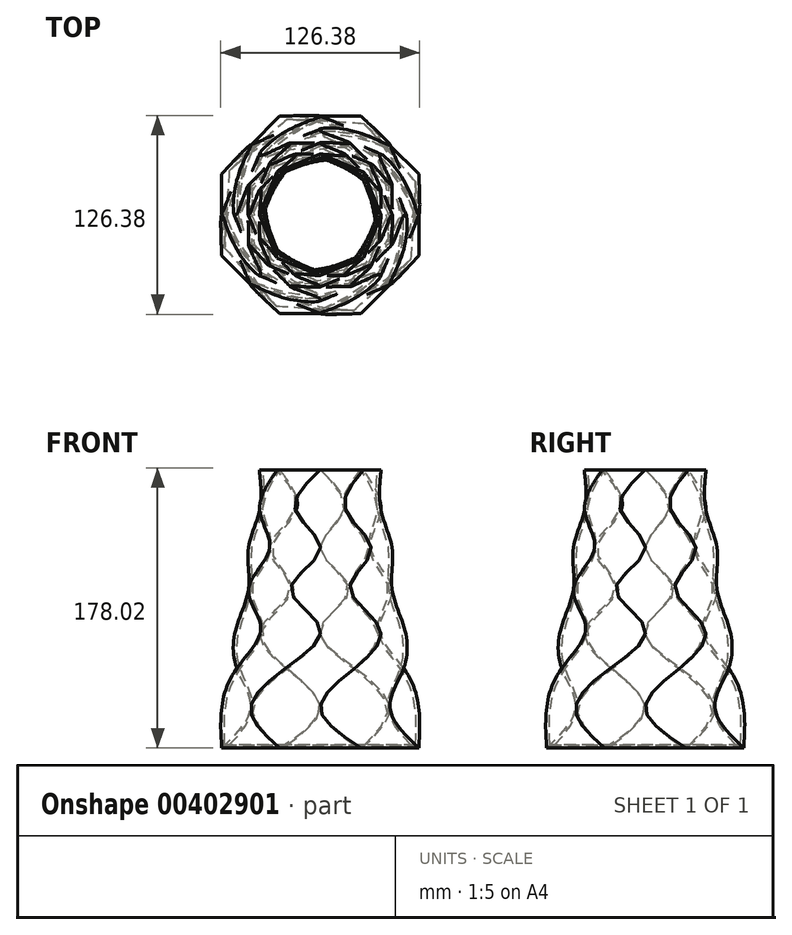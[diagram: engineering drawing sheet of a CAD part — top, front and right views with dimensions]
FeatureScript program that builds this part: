
annotation { "Feature Type Name" : "Feature", "Feature Type Description" : "" }
export const myFeature = defineFeature(function(context is Context, id is Id, definition is map)
    precondition{}
    {
        {
            var Q0;
            Q0=qCreatedBy(makeId("Top.planeOp"),FACE);
            var sketch = newSketch(context, id + "F0", { "sketchPlane" : qUnion([Q0])});
            skCircle(sketch, "E0.cCircle", {"center": v(0, 0) * mm, "radius": 62.6 * mm, "construction": true});
            skLineSegment(sketch, "E0.0", {"start": v(-62.6, -25.93) * mm, "end": v(-62.6, 25.93) * mm});
            skLineSegment(sketch, "E0.1", {"start": v(-62.6, 25.93) * mm, "end": v(-25.93, 62.6) * mm});
            skLineSegment(sketch, "E0.2", {"start": v(-25.93, 62.6) * mm, "end": v(25.93, 62.6) * mm});
            skLineSegment(sketch, "E0.3", {"start": v(25.93, 62.6) * mm, "end": v(62.6, 25.93) * mm});
            skLineSegment(sketch, "E0.4", {"start": v(62.6, 25.93) * mm, "end": v(62.6, -25.93) * mm});
            skLineSegment(sketch, "E0.5", {"start": v(62.6, -25.93) * mm, "end": v(25.93, -62.6) * mm});
            skLineSegment(sketch, "E0.6", {"start": v(25.93, -62.6) * mm, "end": v(-25.93, -62.6) * mm});
            skLineSegment(sketch, "E0.7", {"start": v(-25.93, -62.6) * mm, "end": v(-62.6, -25.93) * mm});
            skPoint(sketch, "E0.0.midPoint", {"position": v(-62.6, 0) * mm});
            skSolve(sketch);
        }
        {
            var Q0;
            Q0=qCreatedBy(makeId("Top.planeOp"),FACE);
            cPlane(context, id + "F1", {"entities" : qUnion([Q0]), "cplaneType" : CPlaneType.OFFSET, "offset" : 25.4 * mm, "width" : 152.4 * mm, "height" : 152.4 * mm});
        }
        {
            var Q0;
            Q0=qCreatedBy(id+"F1.planeOp",FACE);
            var sketch = newSketch(context, id + "F2", { "sketchPlane" : qUnion([Q0])});
            skCircle(sketch, "E1.cCircle", {"center": v(0, 0) * mm, "radius": 57.82 * mm, "construction": true});
            skLineSegment(sketch, "E1.0", {"start": v(44.26, -44.26) * mm, "end": v(0, -62.59) * mm});
            skLineSegment(sketch, "E1.1", {"start": v(0, -62.59) * mm, "end": v(-44.26, -44.26) * mm});
            skLineSegment(sketch, "E1.2", {"start": v(-44.26, -44.26) * mm, "end": v(-62.59, 0) * mm});
            skLineSegment(sketch, "E1.3", {"start": v(-62.59, 0) * mm, "end": v(-44.26, 44.26) * mm});
            skLineSegment(sketch, "E1.4", {"start": v(-44.26, 44.26) * mm, "end": v(0, 62.59) * mm});
            skLineSegment(sketch, "E1.5", {"start": v(0, 62.59) * mm, "end": v(44.26, 44.26) * mm});
            skLineSegment(sketch, "E1.6", {"start": v(44.26, 44.26) * mm, "end": v(62.59, 0) * mm});
            skLineSegment(sketch, "E1.7", {"start": v(62.59, 0) * mm, "end": v(44.26, -44.26) * mm});
            skPoint(sketch, "E1.0.midPoint", {"position": v(22.13, -53.42) * mm});
            skSolve(sketch);
        }
        {
            var Q0;
            Q0=qCreatedBy(id+"F1.planeOp",FACE);
            cPlane(context, id + "F3", {"entities" : qUnion([Q0]), "cplaneType" : CPlaneType.OFFSET, "offset" : 25.4 * mm, "width" : 152.4 * mm, "height" : 152.4 * mm});
        }
        {
            var Q0;
            Q0=qCreatedBy(id+"F3.planeOp",FACE);
            var sketch = newSketch(context, id + "F4", { "sketchPlane" : qUnion([Q0])});
            skCircle(sketch, "E2.cCircle", {"center": v(0, 0) * mm, "radius": 53 * mm, "construction": true});
            skLineSegment(sketch, "E2.0", {"start": v(53, 21.95) * mm, "end": v(53, -21.95) * mm});
            skLineSegment(sketch, "E2.1", {"start": v(53, -21.95) * mm, "end": v(21.95, -53) * mm});
            skLineSegment(sketch, "E2.2", {"start": v(21.95, -53) * mm, "end": v(-21.95, -53) * mm});
            skLineSegment(sketch, "E2.3", {"start": v(-21.95, -53) * mm, "end": v(-53, -21.95) * mm});
            skLineSegment(sketch, "E2.4", {"start": v(-53, -21.95) * mm, "end": v(-53, 21.95) * mm});
            skLineSegment(sketch, "E2.5", {"start": v(-53, 21.95) * mm, "end": v(-21.95, 53) * mm});
            skLineSegment(sketch, "E2.6", {"start": v(-21.95, 53) * mm, "end": v(21.95, 53) * mm});
            skLineSegment(sketch, "E2.7", {"start": v(21.95, 53) * mm, "end": v(53, 21.95) * mm});
            skPoint(sketch, "E2.0.midPoint", {"position": v(53, 0) * mm});
            skSolve(sketch);
        }
        {
            var Q0;
            Q0=qCreatedBy(id+"F3.planeOp",FACE);
            cPlane(context, id + "F5", {"entities" : qUnion([Q0]), "cplaneType" : CPlaneType.OFFSET, "offset" : 25.4 * mm, "width" : 152.4 * mm, "height" : 152.4 * mm});
        }
        {
            var Q0;
            Q0=qCreatedBy(id+"F5.planeOp",FACE);
            var sketch = newSketch(context, id + "F6", { "sketchPlane" : qUnion([Q0])});
            skCircle(sketch, "E3.cCircle", {"center": v(0, 0) * mm, "radius": 49.36 * mm, "construction": true});
            skLineSegment(sketch, "E3.0", {"start": v(53.43, 0) * mm, "end": v(37.78, -37.78) * mm});
            skLineSegment(sketch, "E3.1", {"start": v(37.78, -37.78) * mm, "end": v(0, -53.43) * mm});
            skLineSegment(sketch, "E3.2", {"start": v(0, -53.43) * mm, "end": v(-37.78, -37.78) * mm});
            skLineSegment(sketch, "E3.3", {"start": v(-37.78, -37.78) * mm, "end": v(-53.43, 0) * mm});
            skLineSegment(sketch, "E3.4", {"start": v(-53.43, 0) * mm, "end": v(-37.78, 37.78) * mm});
            skLineSegment(sketch, "E3.5", {"start": v(-37.78, 37.78) * mm, "end": v(0, 53.43) * mm});
            skLineSegment(sketch, "E3.6", {"start": v(0, 53.43) * mm, "end": v(37.78, 37.78) * mm});
            skLineSegment(sketch, "E3.7", {"start": v(37.78, 37.78) * mm, "end": v(53.43, 0) * mm});
            skPoint(sketch, "E3.0.midPoint", {"position": v(45.6, -18.89) * mm});
            skSolve(sketch);
        }
        {
            var Q0;
            Q0=qCreatedBy(id+"F5.planeOp",FACE);
            cPlane(context, id + "F7", {"entities" : qUnion([Q0]), "cplaneType" : CPlaneType.OFFSET, "offset" : 25.4 * mm, "width" : 152.4 * mm, "height" : 152.4 * mm});
        }
        {
            var Q0;
            Q0=qCreatedBy(id+"F7.planeOp",FACE);
            var sketch = newSketch(context, id + "F8", { "sketchPlane" : qUnion([Q0])});
            skCircle(sketch, "E4.cCircle", {"center": v(0, 0) * mm, "radius": 45.49 * mm, "construction": true});
            skLineSegment(sketch, "E4.0", {"start": v(-45.49, -18.84) * mm, "end": v(-45.49, 18.84) * mm});
            skLineSegment(sketch, "E4.1", {"start": v(-45.49, 18.84) * mm, "end": v(-18.84, 45.49) * mm});
            skLineSegment(sketch, "E4.2", {"start": v(-18.84, 45.49) * mm, "end": v(18.84, 45.49) * mm});
            skLineSegment(sketch, "E4.3", {"start": v(18.84, 45.49) * mm, "end": v(45.49, 18.84) * mm});
            skLineSegment(sketch, "E4.4", {"start": v(45.49, 18.84) * mm, "end": v(45.49, -18.84) * mm});
            skLineSegment(sketch, "E4.5", {"start": v(45.49, -18.84) * mm, "end": v(18.84, -45.49) * mm});
            skLineSegment(sketch, "E4.6", {"start": v(18.84, -45.49) * mm, "end": v(-18.84, -45.49) * mm});
            skLineSegment(sketch, "E4.7", {"start": v(-18.84, -45.49) * mm, "end": v(-45.49, -18.84) * mm});
            skPoint(sketch, "E4.0.midPoint", {"position": v(-45.49, 0) * mm});
            skSolve(sketch);
        }
        {
            var Q0;
            Q0=qCreatedBy(id+"F7.planeOp",FACE);
            cPlane(context, id + "F9", {"entities" : qUnion([Q0]), "cplaneType" : CPlaneType.OFFSET, "offset" : 25 * mm, "width" : 150 * mm, "height" : 150 * mm});
        }
        {
            var Q0;
            Q0=qCreatedBy(id+"F9.planeOp",FACE);
            var sketch = newSketch(context, id + "F10", { "sketchPlane" : qUnion([Q0])});
            skCircle(sketch, "E5.cCircle", {"center": v(0, 0) * mm, "radius": 42.19 * mm, "construction": true});
            skLineSegment(sketch, "E5.0", {"start": v(-32.3, 32.3) * mm, "end": v(0, 45.67) * mm});
            skLineSegment(sketch, "E5.1", {"start": v(0, 45.67) * mm, "end": v(32.3, 32.3) * mm});
            skLineSegment(sketch, "E5.2", {"start": v(32.3, 32.3) * mm, "end": v(45.67, 0) * mm});
            skLineSegment(sketch, "E5.3", {"start": v(45.67, 0) * mm, "end": v(32.3, -32.3) * mm});
            skLineSegment(sketch, "E5.4", {"start": v(32.3, -32.3) * mm, "end": v(0, -45.67) * mm});
            skLineSegment(sketch, "E5.5", {"start": v(0, -45.67) * mm, "end": v(-32.3, -32.3) * mm});
            skLineSegment(sketch, "E5.6", {"start": v(-32.3, -32.3) * mm, "end": v(-45.67, 0) * mm});
            skLineSegment(sketch, "E5.7", {"start": v(-45.67, 0) * mm, "end": v(-32.3, 32.3) * mm});
            skPoint(sketch, "E5.0.midPoint", {"position": v(-16.15, 38.98) * mm});
            skSolve(sketch);
        }
        {
            var Q0;
            Q0=qCreatedBy(id+"F9.planeOp",FACE);
            cPlane(context, id + "F11", {"entities" : qUnion([Q0]), "cplaneType" : CPlaneType.OFFSET, "offset" : 25 * mm, "width" : 150 * mm, "height" : 150 * mm});
        }
        {
            var Q0;
            Q0=qCreatedBy(id+"F11.planeOp",FACE);
            var sketch = newSketch(context, id + "F12", { "sketchPlane" : qUnion([Q0])});
            skCircle(sketch, "E6.cCircle", {"center": v(0, 0) * mm, "radius": 38.5 * mm, "construction": true});
            skLineSegment(sketch, "E6.0", {"start": v(-38.5, -15.95) * mm, "end": v(-38.5, 15.95) * mm});
            skLineSegment(sketch, "E6.1", {"start": v(-38.5, 15.95) * mm, "end": v(-15.95, 38.5) * mm});
            skLineSegment(sketch, "E6.2", {"start": v(-15.95, 38.5) * mm, "end": v(15.95, 38.5) * mm});
            skLineSegment(sketch, "E6.3", {"start": v(15.95, 38.5) * mm, "end": v(38.5, 15.95) * mm});
            skLineSegment(sketch, "E6.4", {"start": v(38.5, 15.95) * mm, "end": v(38.5, -15.95) * mm});
            skLineSegment(sketch, "E6.5", {"start": v(38.5, -15.95) * mm, "end": v(15.95, -38.5) * mm});
            skLineSegment(sketch, "E6.6", {"start": v(15.95, -38.5) * mm, "end": v(-15.95, -38.5) * mm});
            skLineSegment(sketch, "E6.7", {"start": v(-15.95, -38.5) * mm, "end": v(-38.5, -15.95) * mm});
            skPoint(sketch, "E6.0.midPoint", {"position": v(-38.5, 0) * mm});
            skSolve(sketch);
        }
        {
            var Q0;
            Q0=qCreatedBy(id+"F11.planeOp",FACE);
            cPlane(context, id + "F13", {"entities" : qUnion([Q0]), "cplaneType" : CPlaneType.OFFSET, "offset" : 25 * mm, "width" : 150 * mm, "height" : 150 * mm});
        }
        {
            var Q0;
            Q0=qCreatedBy(id+"F13.planeOp",FACE);
            var sketch = newSketch(context, id + "F14", { "sketchPlane" : qUnion([Q0])});
            skCircle(sketch, "E7.cCircle", {"center": v(0, 0) * mm, "radius": 35.73 * mm, "construction": true});
            skLineSegment(sketch, "E7.0", {"start": v(-27.35, 27.35) * mm, "end": v(0, 38.67) * mm});
            skLineSegment(sketch, "E7.1", {"start": v(0, 38.67) * mm, "end": v(27.35, 27.35) * mm});
            skLineSegment(sketch, "E7.2", {"start": v(27.35, 27.35) * mm, "end": v(38.67, 0) * mm});
            skLineSegment(sketch, "E7.3", {"start": v(38.67, 0) * mm, "end": v(27.35, -27.35) * mm});
            skLineSegment(sketch, "E7.4", {"start": v(27.35, -27.35) * mm, "end": v(0, -38.67) * mm});
            skLineSegment(sketch, "E7.5", {"start": v(0, -38.67) * mm, "end": v(-27.35, -27.35) * mm});
            skLineSegment(sketch, "E7.6", {"start": v(-27.35, -27.35) * mm, "end": v(-38.67, 0) * mm});
            skLineSegment(sketch, "E7.7", {"start": v(-38.67, 0) * mm, "end": v(-27.35, 27.35) * mm});
            skPoint(sketch, "E7.0.midPoint", {"position": v(-13.67, 33) * mm});
            skSolve(sketch);
        }
        {
            var Q0;
            Q0=makeQuery(id+"F0.imprint","IMPRINT",FACE,{"disambiguationData":[TD([[makeQuery(id+"F0.imprint","IMPRINT",EDGE,{"derivedFrom":sQuery(id+"F0.wireOp",EDGE,"E0.0")}),-1.0]])]});
            var Q1;
            Q1=makeQuery(id+"F2.imprint","IMPRINT",FACE,{"disambiguationData":[TD([[makeQuery(id+"F2.imprint","IMPRINT",EDGE,{"derivedFrom":sQuery(id+"F2.wireOp",EDGE,"E1.0")}),-1.0]])]});
            var Q2;
            Q2=makeQuery(id+"F4.imprint","IMPRINT",FACE,{"disambiguationData":[TD([[makeQuery(id+"F4.imprint","IMPRINT",EDGE,{"derivedFrom":sQuery(id+"F4.wireOp",EDGE,"E2.0")}),-1.0]])]});
            var Q3;
            Q3=makeQuery(id+"F6.imprint","IMPRINT",FACE,{"disambiguationData":[TD([[makeQuery(id+"F6.imprint","IMPRINT",EDGE,{"derivedFrom":sQuery(id+"F6.wireOp",EDGE,"E3.0")}),-1.0]])]});
            var Q4;
            Q4=makeQuery(id+"F8.imprint","IMPRINT",FACE,{"disambiguationData":[TD([[makeQuery(id+"F8.imprint","IMPRINT",EDGE,{"derivedFrom":sQuery(id+"F8.wireOp",EDGE,"E4.0")}),-1.0]])]});
            var Q5;
            Q5=makeQuery(id+"F10.imprint","IMPRINT",FACE,{"disambiguationData":[TD([[makeQuery(id+"F10.imprint","IMPRINT",EDGE,{"derivedFrom":sQuery(id+"F10.wireOp",EDGE,"E5.0")}),-1.0]])]});
            var Q6;
            Q6=makeQuery(id+"F12.imprint","IMPRINT",FACE,{"disambiguationData":[TD([[makeQuery(id+"F12.imprint","IMPRINT",EDGE,{"derivedFrom":sQuery(id+"F12.wireOp",EDGE,"E6.0")}),-1.0]])]});
            var Q7;
            Q7=makeQuery(id+"F14.imprint","IMPRINT",FACE,{"disambiguationData":[TD([[makeQuery(id+"F14.imprint","IMPRINT",EDGE,{"derivedFrom":sQuery(id+"F14.wireOp",EDGE,"E7.0")}),-1.0]])]});
            loft(context, id + "F15", {"sheetProfilesArray" : [{ "sheetProfileEntities" : qUnion([Q0]) }, { "sheetProfileEntities" : qUnion([Q1]) }, { "sheetProfileEntities" : qUnion([Q2]) }, { "sheetProfileEntities" : qUnion([Q3]) }, { "sheetProfileEntities" : qUnion([Q4]) }, { "sheetProfileEntities" : qUnion([Q5]) }, { "sheetProfileEntities" : qUnion([Q6]) }, { "sheetProfileEntities" : qUnion([Q7]) }]});
        }
        {
            var Q0;
            Q0=makeQuery(id+"F15.opLoft","CAP_FACE",FACE,{"disambiguationData":[OSD([makeQuery(id+"F14.imprint","IMPRINT",FACE,{"disambiguationData":[TD([[makeQuery(id+"F14.imprint","IMPRINT",EDGE,{"derivedFrom":sQuery(id+"F14.wireOp",EDGE,"E7.0")}),-1.0]])]})])],"isStart":true});
            shell(context, id + "F16", {"entities" : qUnion([Q0]), "thickness" : 2 * mm});
        }
    });
